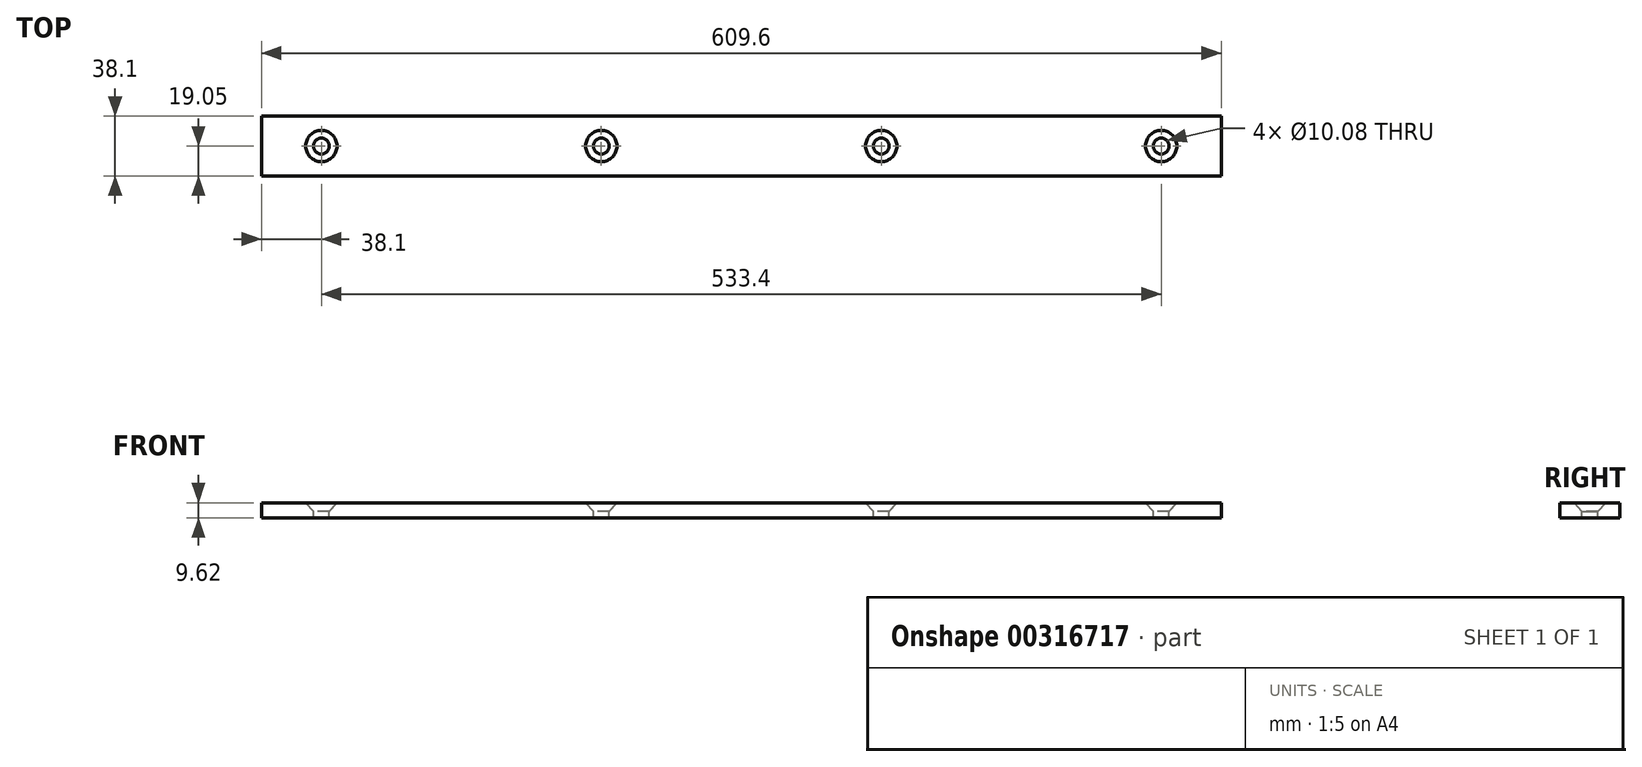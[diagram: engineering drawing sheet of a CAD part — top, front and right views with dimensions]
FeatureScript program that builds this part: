
annotation { "Feature Type Name" : "Feature", "Feature Type Description" : "" }
export const myFeature = defineFeature(function(context is Context, id is Id, definition is map)
    precondition{}
    {
        {
            var Q0;
            Q0=qCreatedBy(makeId("Top.planeOp"),FACE);
            var sketch = newSketch(context, id + "F0", { "sketchPlane" : qUnion([Q0])});
            skLineSegment(sketch, "E0.bottom", {"start": v(-304.8, 19.05) * mm, "end": v(304.8, 19.05) * mm});
            skLineSegment(sketch, "E0.top", {"start": v(-304.8, -19.05) * mm, "end": v(304.8, -19.05) * mm});
            skLineSegment(sketch, "E0.left", {"start": v(-304.8, 19.05) * mm, "end": v(-304.8, -19.05) * mm});
            skLineSegment(sketch, "E0.right", {"start": v(304.8, 19.05) * mm, "end": v(304.8, -19.05) * mm});
            skPoint(sketch, "E0.middle", {"position": v(0, 0) * mm});
            skSolve(sketch);
        }
        {
            var Q0;
            Q0 = qSketchRegion(id + "F0", true);
            extrude(context, id + "F1", {"entities" : qUnion([Q0]), "endBound" : BoundingType.SYMMETRIC, "depth" : 9.63 * mm});
        }
        {
            var Q0;
            Q0=makeQuery(id+"F1.opExtrude","CAP_FACE",FACE,{"disambiguationData":[OSD([sQuery(id+"F0.wireOp",EDGE,"E0.bottom"),sQuery(id+"F0.wireOp",EDGE,"E0.top"),sQuery(id+"F0.wireOp",EDGE,"E0.left"),sQuery(id+"F0.wireOp",EDGE,"E0.right")])],"isStart":false});
            var sketch = newSketch(context, id + "F2", { "sketchPlane" : qUnion([Q0])});
            skLineSegment(sketch, "E1.0", {"start": v(-266.7, 19.05) * mm, "end": v(-266.7, -19.05) * mm, "construction": true});
            skLineSegment(sketch, "E2.0", {"start": v(-88.9, 19.05) * mm, "end": v(-88.9, -19.05) * mm, "construction": true});
            skLineSegment(sketch, "E3.0", {"start": v(88.9, 19.05) * mm, "end": v(88.9, -19.05) * mm, "construction": true});
            skLineSegment(sketch, "E4.0", {"start": v(266.7, 19.05) * mm, "end": v(266.7, -19.05) * mm, "construction": true});
            skLineSegment(sketch, "E5", {"start": v(-266.7, 0) * mm, "end": v(266.7, 0) * mm, "construction": true});
            skPoint(sketch, "E6", {"position": v(-266.7, 0) * mm});
            skPoint(sketch, "E7", {"position": v(-88.9, 0) * mm});
            skPoint(sketch, "E8", {"position": v(88.9, 0) * mm});
            skPoint(sketch, "E9", {"position": v(266.7, 0) * mm});
            skSolve(sketch);
        }
        {
            var Q0;
            Q0=sQuery(id+"F2.wireOp",VERTEX,"E6");
            var Q1;
            Q1=sQuery(id+"F2.wireOp",VERTEX,"E7");
            var Q2;
            Q2=sQuery(id+"F2.wireOp",VERTEX,"E8");
            var Q3;
            Q3=sQuery(id+"F2.wireOp",VERTEX,"E9");
            var Q4;
            Q4=makeQuery(id+"F1.opExtrude","SWEPT_BODY",BODY,{"disambiguationData":[OSD([sQuery(id+"F0.wireOp",EDGE,"E0.bottom"),sQuery(id+"F0.wireOp",EDGE,"E0.top"),sQuery(id+"F0.wireOp",EDGE,"E0.left"),sQuery(id+"F0.wireOp",EDGE,"E0.right")])]});
            hole(context, id + "F3", {"style" : HoleStyle.C_SINK, "endStyle" : HoleEndStyle.THROUGH, "standardTappedOrClearance" : lookupTablePath({ "standard" : "ANSI", "fit" : "Normal (ASME)", "size" : "3/8", "type" : "Clearance" }), "standardBlindInLast" : lookupTablePath({ "fit" : "Free", "standard" : "ANSI", "size" : "3/8", "type" : "Clearance" }), "holeDiameter" : 10.08 * mm, "cSinkDiameter" : 19.84 * mm, "cSinkAngle" : 82 * degree, "tappedDepth" : 14.29 * mm, "tapClearance" : 3, "locations" : qUnion([Q0, Q1, Q2, Q3]), "scope" : qUnion([Q4])});
        }
    });
